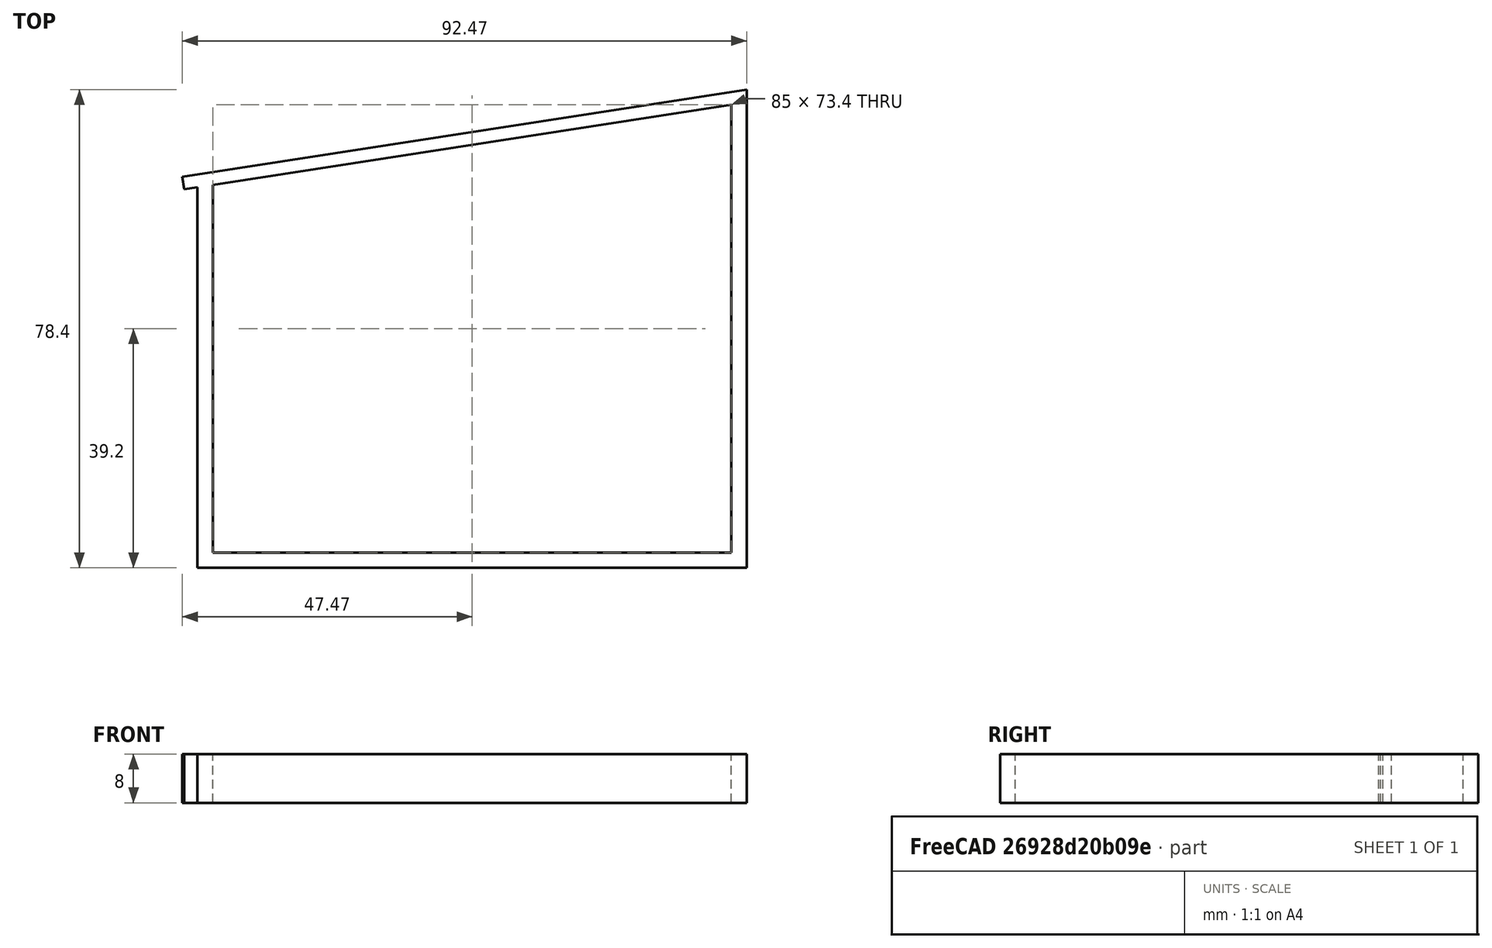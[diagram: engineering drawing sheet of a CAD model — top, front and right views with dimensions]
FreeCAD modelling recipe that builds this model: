
FCSTD DOCUMENT  (FreeCAD 1.0R39109 (Git))
Label: Gerüst-Fuß-rechts-DerGerät
License: All rights reserved
LicenseURL: https://en.wikipedia.org/wiki/All_rights_reserved
objects: Sketcher::SketchObject×1, PartDesign::Pad×1, PartDesign::Body×1
note: 6 computed .brp shape members not serialized (recipe doc carries the construction recipe); baked Part::Feature solids carry a one-line shape summary decoded from their .brp

FEATURE [Sketcher::SketchObject] Sketch
  ArcFitTolerance = 1e-06
  AttachmentSupport = -> [XY_Plane]
  FullyConstrained = true
  MakeInternals = false
  MapMode = 5
  sketch-geometry (12):
    g0: LineSegment StartX=0 StartY=0 StartZ=0 EndX=0 EndY=62.3861 EndZ=0
    g1: LineSegment StartX=0 StartY=64.5 StartZ=0 EndX=90 EndY=78.4 EndZ=0
    g2: LineSegment StartX=90 StartY=78.4 StartZ=0 EndX=90 EndY=0 EndZ=0
    g3: LineSegment StartX=90 StartY=0 StartZ=0 EndX=0 EndY=0 EndZ=0
    g4: LineSegment StartX=2.5 StartY=2.5 StartZ=0 EndX=87.5 EndY=2.5 EndZ=0
    g5: LineSegment StartX=87.5 StartY=2.5 StartZ=0 EndX=87.5 EndY=75.9 EndZ=0
    g6: LineSegment StartX=87.5 StartY=75.9 StartZ=0 EndX=2.5 EndY=62.7722 EndZ=0
    g7: LineSegment StartX=2.5 StartY=62.7722 StartZ=0 EndX=2.5 EndY=2.5 EndZ=0
    g8: LineSegment StartX=0 StartY=64.5 StartZ=0 EndX=-2.47071 EndY=64.1184 EndZ=0
    g9: LineSegment StartX=-2.47071 StartY=64.1184 StartZ=0 EndX=-2.15183 EndY=62.0538 EndZ=0
    g10: LineSegment StartX=-2.15183 StartY=62.0538 StartZ=0 EndX=0 EndY=62.3861 EndZ=0
    g11: LineSegment [constr] StartX=0 StartY=62.3861 StartZ=0 EndX=2.5 EndY=62.7722 EndZ=0
  constraints (34):
    c: Coincident(g-1,g0)
    c: PointOnObject(g1,g-2)
    c: Coincident(g1,g2)
    c: PointOnObject(g2,g-1)
    c: Vertical(g2)
    c: Coincident(g2,g3)
    c: Coincident(g3,g0)
    c: DistanceX(g3,g3) = 90
    c: DistanceY(g0,g1) = 64.5
    c: DistanceY(g2,g2) = 78.4
    c: Horizontal(g4)
    c: Coincident(g4,g5)
    c: Vertical(g5)
    c: Coincident(g5,g6)
    c: Coincident(g6,g7)
    c: Coincident(g7,g4)
    c: Vertical(g7)
    c: Distance(g0,g7) = 2.5
    c: Parallel(g1,g6)
    c: Distance(g2,g5) = 2.5
    c: DistanceY(g5,g5) = 73.4
    c: Distance(g3,g4) = 2.5
    c: Coincident(g8,g1)
    c: Coincident(g9,g8)
    c: Parallel(g1,g8)
    c: Perpendicular(g8,g9)
    c: Distance(g8,g8) = 2.5
    c: Coincident(g10,g9)
    c: Coincident(g10,g0)
    c: Vertical(g0)
    c: Parallel(g10,g8)
    c: Coincident(g11,g0)
    c: Coincident(g11,g6)
    c: Parallel(g11,g6)
FEATURE [PartDesign::Pad] Pad
  Direction = (0,0,1)
  Length = 8
  Length2 = 10
  Profile = -> Sketch
  ReferenceAxis = -> Sketch [N_Axis]
  Refine = true
  Suppressed = false
  Type = 0
FEATURE [PartDesign::Body] Body  label="Körper"
  AllowCompound = false
  Group = -> [Sketch,Pad]
  Origin = -> Origin
  Tip = -> Pad
